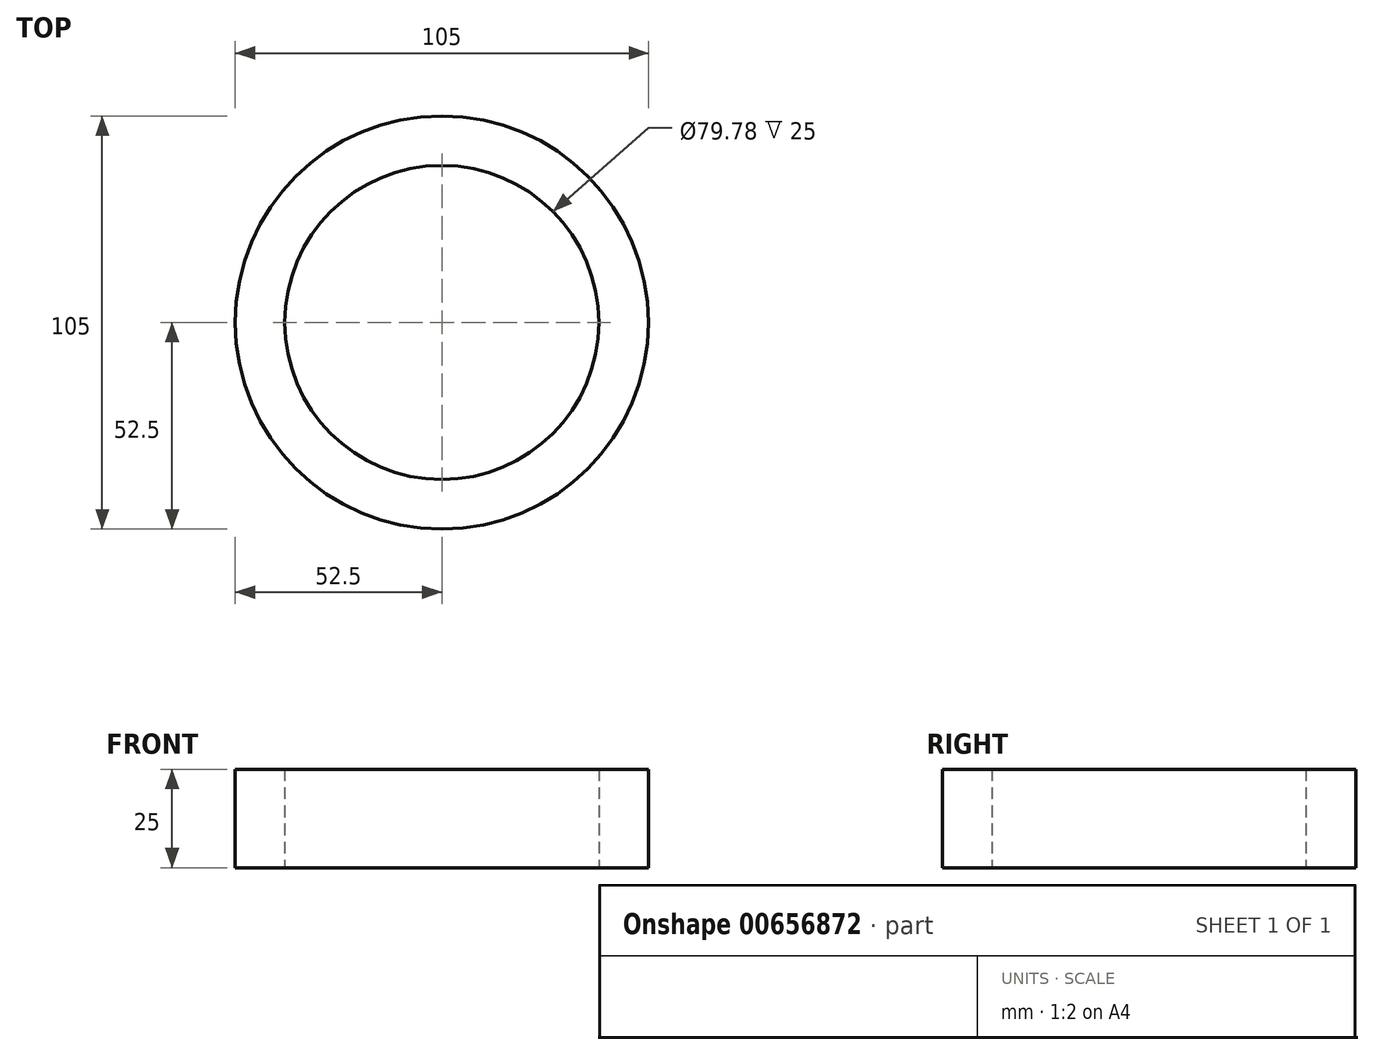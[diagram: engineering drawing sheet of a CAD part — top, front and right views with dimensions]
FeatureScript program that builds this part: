
annotation { "Feature Type Name" : "Feature", "Feature Type Description" : "" }
export const myFeature = defineFeature(function(context is Context, id is Id, definition is map)
    precondition{}
    {
        {
            var Q0;
            Q0=qCreatedBy(makeId("Top.planeOp"),FACE);
            var sketch = newSketch(context, id + "F0", { "sketchPlane" : qUnion([Q0])});
            skCircle(sketch, "E0", {"center": v(0, 0) * mm, "radius": 52.5 * mm});
            skCircle(sketch, "E1", {"center": v(0, 0) * mm, "radius": 39.89 * mm});
            skSolve(sketch);
        }
        {
            var Q0;
            Q0=makeQuery(id+"F0.imprint","IMPRINT",FACE,{"disambiguationData":[TD([[makeQuery(id+"F0.imprint","IMPRINT",EDGE,{"derivedFrom":sQuery(id+"F0.wireOp",EDGE,"E0")}),1.0]])]});
            extrude(context, id + "F1", {"entities" : qUnion([Q0]), "depth" : 25 * mm, "offsetDistance" : 25 * mm});
        }
    });
